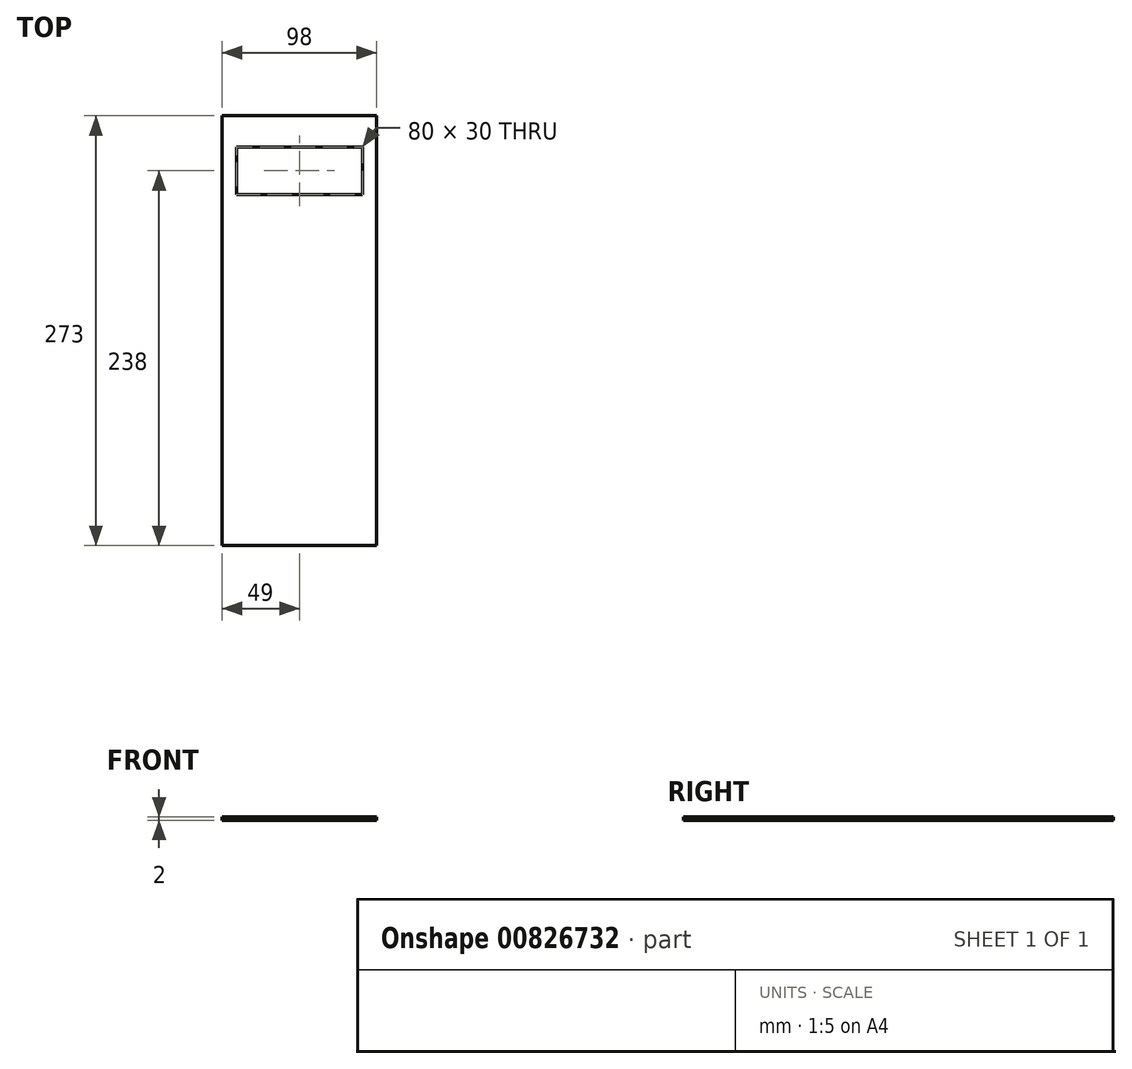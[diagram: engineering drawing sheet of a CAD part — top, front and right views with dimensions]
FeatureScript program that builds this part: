
annotation { "Feature Type Name" : "Feature", "Feature Type Description" : "" }
export const myFeature = defineFeature(function(context is Context, id is Id, definition is map)
    precondition{}
    {
        {
            var Q0;
            Q0=qCreatedBy(makeId("Top.planeOp"),FACE);
            var sketch = newSketch(context, id + "F0", { "sketchPlane" : qUnion([Q0])});
            skLineSegment(sketch, "E0.bottom", {"start": v(49, 136.5) * mm, "end": v(-49, 136.5) * mm});
            skLineSegment(sketch, "E0.top", {"start": v(49, -136.5) * mm, "end": v(-49, -136.5) * mm});
            skLineSegment(sketch, "E0.left", {"start": v(49, 136.5) * mm, "end": v(49, -136.5) * mm});
            skLineSegment(sketch, "E0.right", {"start": v(-49, 136.5) * mm, "end": v(-49, -136.5) * mm});
            skPoint(sketch, "E0.middle", {"position": v(0, 0) * mm});
            skLineSegment(sketch, "E1.bottom", {"start": v(40, 86.5) * mm, "end": v(-40, 86.5) * mm});
            skLineSegment(sketch, "E1.top", {"start": v(40, 116.5) * mm, "end": v(-40, 116.5) * mm});
            skLineSegment(sketch, "E1.left", {"start": v(40, 86.5) * mm, "end": v(40, 116.5) * mm});
            skLineSegment(sketch, "E1.right", {"start": v(-40, 86.5) * mm, "end": v(-40, 116.5) * mm});
            skPoint(sketch, "E1.middle", {"position": v(0, 101.5) * mm});
            skSolve(sketch);
        }
        {
            var Q0;
            Q0=makeQuery(id+"F0.imprint","IMPRINT",FACE,{"disambiguationData":[TD([[makeQuery(id+"F0.imprint","IMPRINT",EDGE,{"derivedFrom":sQuery(id+"F0.wireOp",EDGE,"E0.bottom")}),1.0]])]});
            extrude(context, id + "F1", {"entities" : qUnion([Q0]), "depth" : 2 * mm, "offsetDistance" : 25 * mm});
        }
    });
